# Revit family: QF_Vollrath_CM4-20835PA
name_source: partatom
category: Specialty Equipment
revit_build: Autodesk Revit 2016 (Build: 20151007_0715(x64)
units: mm (PartAtom-declared; Revit-internal decimal feet)

## family parameters
Always vertical = Yes
Cut with Voids When Loaded = No
OmniClass Number = 23.40.40.00
OmniClass Title = Food Service Equipment and Furnishings
Part Type = Normal
Room Calculation Point = No
Round Connector Dimension = Use Diameter
Shared = No
Work Plane-Based = No

## types (1)
- 208/60/1
    Apparent Power = 3661 VA
    Assembly Code = E1090320
    Conn Plug = NEMA 6-30P
    Cycle = 60 Hz
    Depth = 14 3/8"
    Description = Cheese Melter
    Elec Conn Connection Height = 0"
    FL Amps = 18 A
    Foodservice Equipment Identifier = Yes
    Height = 14 3/4"
    Manufacturer = Vollrath
    Model = CM4-20835PA
    Phase = 1
    URL = http://vollrath.com
    Volts = 208 V
    Watts = 3660 W
    Weight in Pounds = 60
    Width = 35 1/8"

## geometry (parser evidence)
native form markers: Sweep x2
no freeform markers — native parametric forms only
